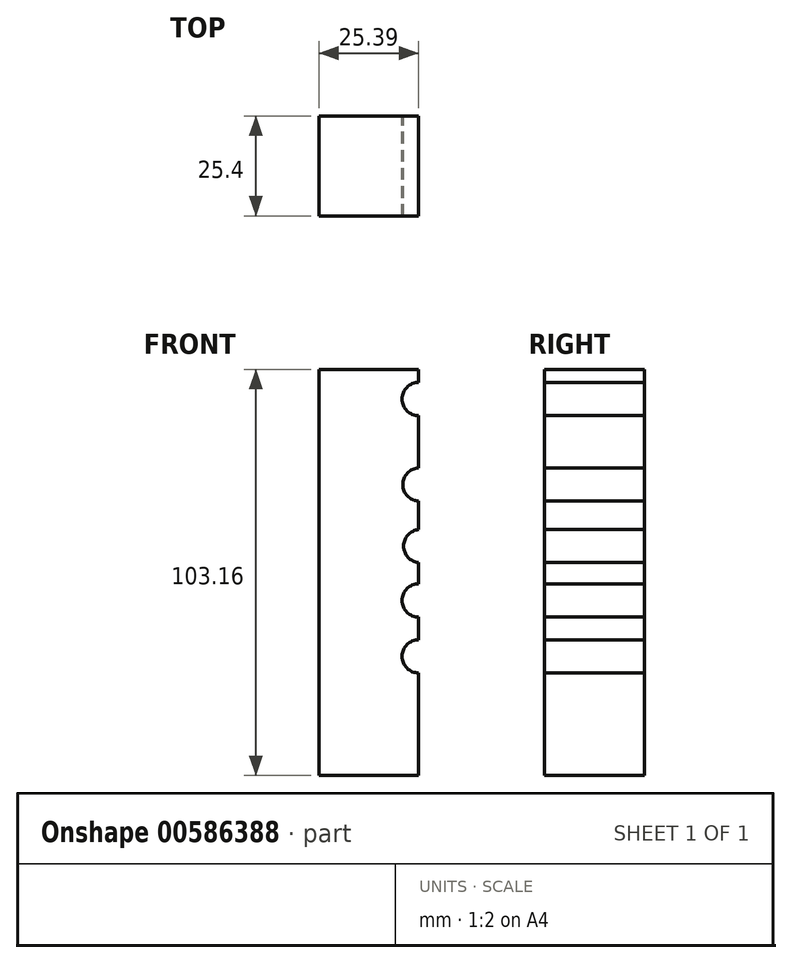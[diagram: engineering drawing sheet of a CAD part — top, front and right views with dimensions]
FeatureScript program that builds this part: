
annotation { "Feature Type Name" : "Feature", "Feature Type Description" : "" }
export const myFeature = defineFeature(function(context is Context, id is Id, definition is map)
    precondition{}
    {
        {
            var Q0;
            Q0=qCreatedBy(makeId("Front.planeOp"),FACE);
            var sketch = newSketch(context, id + "F0", { "sketchPlane" : qUnion([Q0])});
            skLineSegment(sketch, "E0.bottom", {"start": v(-42.75, 52.5) * mm, "end": v(-17.36, 52.5) * mm});
            skLineSegment(sketch, "E0.top", {"start": v(-42.75, -50.67) * mm, "end": v(-17.36, -50.67) * mm});
            skLineSegment(sketch, "E0.left", {"start": v(-42.75, 52.5) * mm, "end": v(-42.75, -50.67) * mm});
            skLineSegment(sketch, "E0.right", {"start": v(-17.36, 52.5) * mm, "end": v(-17.36, 49.2) * mm});
            skCircle(sketch, "E1", {"center": v(-17.36, 44.98) * mm, "radius": 4.23 * mm});
            skCircle(sketch, "E2", {"center": v(-17.16, 23.25) * mm, "radius": 4.23 * mm});
            skCircle(sketch, "E3", {"center": v(-16.96, 7.62) * mm, "radius": 4.23 * mm});
            skCircle(sketch, "E4", {"center": v(-17.36, -6.2) * mm, "radius": 4.23 * mm});
            skCircle(sketch, "E5", {"center": v(-17.36, -20.4) * mm, "radius": 4.23 * mm});
            skLineSegment(sketch, "E6.trimOffspring", {"start": v(-17.36, 40.75) * mm, "end": v(-17.36, 27.47) * mm});
            skLineSegment(sketch, "E7.trimOffspring", {"start": v(-17.36, 19.03) * mm, "end": v(-17.36, 11.82) * mm});
            skLineSegment(sketch, "E8.trimOffspring", {"start": v(-17.36, 3.4) * mm, "end": v(-17.36, -1.97) * mm});
            skLineSegment(sketch, "E9.trimOffspring", {"start": v(-17.36, -10.42) * mm, "end": v(-17.36, -16.18) * mm});
            skLineSegment(sketch, "E10.trimOffspring", {"start": v(-17.36, -24.63) * mm, "end": v(-17.36, -50.67) * mm});
            skSolve(sketch);
        }
        {
            var Q0;
            Q0=makeQuery(id+"F0.imprint","IMPRINT",FACE,{"disambiguationData":[TD([[makeQuery(id+"F0.imprint","IMPRINT",EDGE,{"derivedFrom":sQuery(id+"F0.wireOp",EDGE,"E0.bottom")}),-1.0]])]});
            extrude(context, id + "F1", {"entities" : qUnion([Q0]), "depth" : 25.4 * mm, "offsetDistance" : 25.4 * mm});
        }
    });
